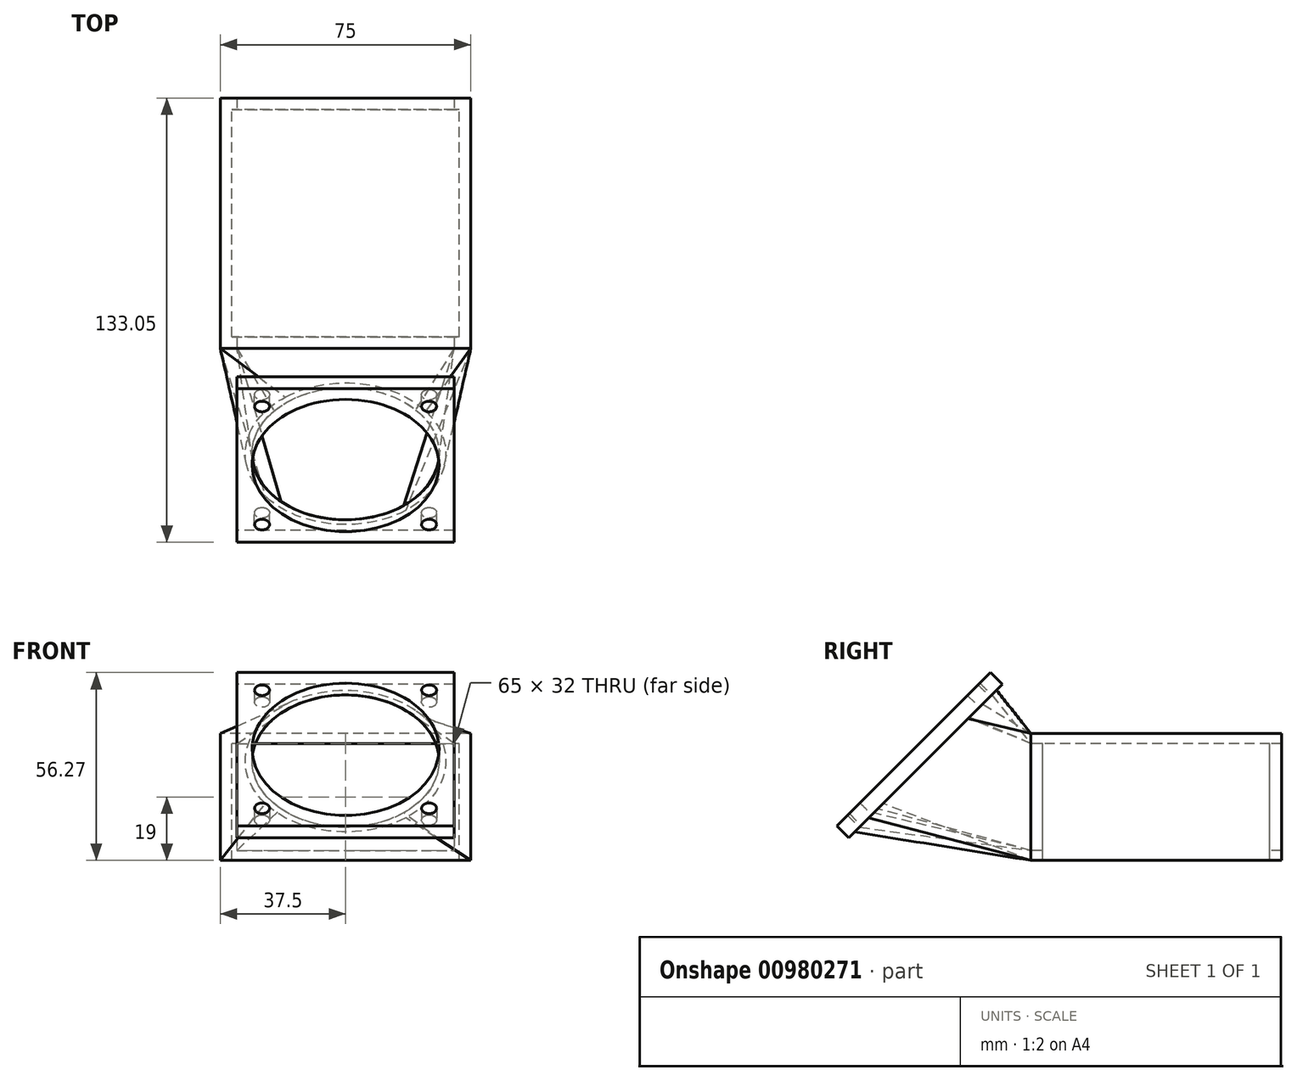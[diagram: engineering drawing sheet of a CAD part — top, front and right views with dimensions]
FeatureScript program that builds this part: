
annotation { "Feature Type Name" : "Feature", "Feature Type Description" : "" }
export const myFeature = defineFeature(function(context is Context, id is Id, definition is map)
    precondition{}
    {
        {
            var Q0;
            Q0=qCreatedBy(makeId("Top.planeOp"),FACE);
            cPlane(context, id + "F0", {"entities" : qUnion([Q0]), "cplaneType" : CPlaneType.OFFSET, "offset" : 3 * mm, "width" : 152.4 * mm, "height" : 152.4 * mm});
        }
        {
            var Q0;
            Q0=qCreatedBy(id+"F0.planeOp",FACE);
            var sketch = newSketch(context, id + "F1", { "sketchPlane" : qUnion([Q0])});
            skLineSegment(sketch, "E0.bottom", {"start": v(37.5, -37.5) * mm, "end": v(-37.5, -37.5) * mm});
            skLineSegment(sketch, "E0.top", {"start": v(37.5, 37.5) * mm, "end": v(-37.5, 37.5) * mm});
            skLineSegment(sketch, "E0.left", {"start": v(37.5, -37.5) * mm, "end": v(37.5, 37.5) * mm});
            skLineSegment(sketch, "E0.right", {"start": v(-37.5, -37.5) * mm, "end": v(-37.5, 37.5) * mm});
            skPoint(sketch, "E0.middle", {"position": v(0, 0) * mm});
            skSolve(sketch);
        }
        {
            var Q0;
            Q0=makeQuery(id+"F1.imprint","IMPRINT",FACE,{"disambiguationData":[TD([[makeQuery(id+"F1.imprint","IMPRINT",EDGE,{"derivedFrom":sQuery(id+"F1.wireOp",EDGE,"E0.bottom")}),-1.0]])]});
            extrude(context, id + "F2", {"entities" : qUnion([Q0]), "oppositeDirection" : true, "depth" : 38 * mm, "offsetDistance" : 25 * mm});
        }
        {
            var Q0;
            Q0=qCreatedBy(makeId("Top.planeOp"),FACE);
            var sketch = newSketch(context, id + "F3", { "sketchPlane" : qUnion([Q0])});
            skPoint(sketch, "E1.middle", {"position": v(0, 0) * mm});
            skLineSegment(sketch, "E2.bottom", {"start": v(34, 34) * mm, "end": v(-34, 34) * mm});
            skLineSegment(sketch, "E2.top", {"start": v(34, -34) * mm, "end": v(-34, -34) * mm});
            skLineSegment(sketch, "E2.left", {"start": v(34, 34) * mm, "end": v(34, -34) * mm});
            skLineSegment(sketch, "E2.right", {"start": v(-34, 34) * mm, "end": v(-34, -34) * mm});
            skSolve(sketch);
        }
        {
            var Q0;
            Q0 = qSketchRegion(id + "F3", true);
            var Q1;
            Q1=makeQuery(id+"F2.opExtrude","CAP_FACE",FACE,{"disambiguationData":[OSD([sQuery(id+"F1.wireOp",EDGE,"E0.bottom"),sQuery(id+"F1.wireOp",EDGE,"E0.top"),sQuery(id+"F1.wireOp",EDGE,"E0.left"),sQuery(id+"F1.wireOp",EDGE,"E0.right")])],"isStart":false});
            extrude(context, id + "F4", {"entities" : qUnion([Q0]), "endBound" : BoundingType.UP_TO_SURFACE, "oppositeDirection" : true, "depth" : 70 * mm, "endBoundEntityFace" : qUnion([Q1]), "offsetDistance" : 25 * mm});
        }
        {
            var Q0;
            Q0=makeQuery(id+"F4.opExtrude","SWEPT_BODY",BODY,{"disambiguationData":[OSD([sQuery(id+"F3.wireOp",EDGE,"E2.bottom"),sQuery(id+"F3.wireOp",EDGE,"E2.top"),sQuery(id+"F3.wireOp",EDGE,"E2.left"),sQuery(id+"F3.wireOp",EDGE,"E2.right")])]});
            var Q1;
            Q1=makeQuery(id+"F2.opExtrude","SWEPT_BODY",BODY,{"disambiguationData":[OSD([sQuery(id+"F1.wireOp",EDGE,"E0.bottom"),sQuery(id+"F1.wireOp",EDGE,"E0.top"),sQuery(id+"F1.wireOp",EDGE,"E0.left"),sQuery(id+"F1.wireOp",EDGE,"E0.right")])]});
            booleanBodies(context, id + "F5", {"operationType" : BooleanOperationType.SUBTRACTION, "tools" : qUnion([Q0]), "targets" : qUnion([Q1])});
        }
        {
            var Q0;
            Q0=makeQuery(id+"F2.opExtrude","SWEPT_FACE",FACE,{"disambiguationData":[OSD([sQuery(id+"F1.wireOp",EDGE,"E0.bottom")])]});
            var sketch = newSketch(context, id + "F6", { "sketchPlane" : qUnion([Q0])});
            skLineSegment(sketch, "E3.bottom", {"start": v(-32.5, 0) * mm, "end": v(32.5, 0) * mm});
            skLineSegment(sketch, "E3.top", {"start": v(-32.5, -32) * mm, "end": v(32.5, -32) * mm});
            skLineSegment(sketch, "E3.left", {"start": v(-32.5, 0) * mm, "end": v(-32.5, -32) * mm});
            skLineSegment(sketch, "E3.right", {"start": v(32.5, 0) * mm, "end": v(32.5, -32) * mm});
            skPoint(sketch, "E3.middle", {"position": v(0, -16) * mm});
            skPoint(sketch, "E3.centerSnap0", {"position": v(36.5, -16) * mm});
            skPoint(sketch, "E3.centerSnap1", {"position": v(0, 32.87) * mm});
            skSolve(sketch);
        }
        {
            var Q0;
            Q0=makeQuery(id+"F6.imprint","IMPRINT",FACE,{"disambiguationData":[TD([[makeQuery(id+"F6.imprint","IMPRINT",EDGE,{"derivedFrom":sQuery(id+"F6.wireOp",EDGE,"E3.bottom")}),-1.0]])]});
            var Q1;
            Q1=makeQuery(id+"F2.opExtrude","SWEPT_FACE",FACE,{"disambiguationData":[OSD([sQuery(id+"F1.wireOp",EDGE,"E0.top")])]});
            extrude(context, id + "F7", {"entities" : qUnion([Q0]), "endBound" : BoundingType.UP_TO_SURFACE, "oppositeDirection" : true, "depth" : 25 * mm, "endBoundEntityFace" : qUnion([Q1]), "offsetDistance" : 25 * mm});
        }
        {
            var Q0;
            Q0=makeQuery(id+"F7.opExtrude","SWEPT_BODY",BODY,{"disambiguationData":[OSD([sQuery(id+"F6.wireOp",EDGE,"E3.bottom"),sQuery(id+"F6.wireOp",EDGE,"E3.top"),sQuery(id+"F6.wireOp",EDGE,"E3.left"),sQuery(id+"F6.wireOp",EDGE,"E3.right")])]});
            var Q1;
            Q1=makeQuery(id+"F2.opExtrude","SWEPT_BODY",BODY,{"disambiguationData":[OSD([sQuery(id+"F1.wireOp",EDGE,"E0.bottom"),sQuery(id+"F1.wireOp",EDGE,"E0.top"),sQuery(id+"F1.wireOp",EDGE,"E0.left"),sQuery(id+"F1.wireOp",EDGE,"E0.right")])]});
            booleanBodies(context, id + "F8", {"operationType" : BooleanOperationType.SUBTRACTION, "tools" : qUnion([Q0]), "targets" : qUnion([Q1])});
        }
        {
            var Q0;
            Q0=makeQuery(id+"F2.opExtrude","SWEPT_FACE",FACE,{"disambiguationData":[OSD([sQuery(id+"F1.wireOp",EDGE,"E0.bottom")])]});
            var sketch = newSketch(context, id + "F9", { "sketchPlane" : qUnion([Q0])});
            skLineSegment(sketch, "E4.bottom", {"start": v(-32.5, -32) * mm, "end": v(32.5, -32) * mm});
            skLineSegment(sketch, "E4.top", {"start": v(-32.5, 0) * mm, "end": v(32.5, 0) * mm});
            skLineSegment(sketch, "E4.left", {"start": v(-32.5, -32) * mm, "end": v(-32.5, 0) * mm});
            skLineSegment(sketch, "E4.right", {"start": v(32.5, -32) * mm, "end": v(32.5, 0) * mm});
            skSolve(sketch);
        }
        {
            var Q0;
            Q0=makeQuery(id+"F2.opExtrude","SWEPT_FACE",FACE,{"disambiguationData":[OSD([sQuery(id+"F1.wireOp",EDGE,"E0.bottom")])]});
            var sketch = newSketch(context, id + "F10", { "sketchPlane" : qUnion([Q0])});
            skLineSegment(sketch, "E5.bottom", {"start": v(-37.5, 3) * mm, "end": v(37.5, 3) * mm});
            skLineSegment(sketch, "E5.top", {"start": v(-37.5, -35) * mm, "end": v(37.5, -35) * mm});
            skLineSegment(sketch, "E5.left", {"start": v(-37.5, 3) * mm, "end": v(-37.5, -35) * mm});
            skLineSegment(sketch, "E5.right", {"start": v(37.5, 3) * mm, "end": v(37.5, -35) * mm});
            skSolve(sketch);
        }
        {
            var Q0;
            Q0=makeQuery(id+"F10.imprint","IMPRINT",FACE,{"disambiguationData":[TD([[makeQuery(id+"F10.imprint","IMPRINT",EDGE,{"derivedFrom":sQuery(id+"F10.wireOp",EDGE,"E5.bottom")}),1.0]])]});
            var sketch = newSketch(context, id + "F11", { "sketchPlane" : qUnion([Q0])});
            skLineSegment(sketch, "E6", {"start": v(-64.88, -2) * mm, "end": v(64.63, -2) * mm, "construction": true});
            skSolve(sketch);
        }
        {
            var Q0;
            Q0=sQuery(id+"F11.wireOp",EDGE,"E6");
            cPlane(context, id + "F12", {"entities" : qUnion([Q0]), "cplaneType" : CPlaneType.LINE_ANGLE, "offset" : 80 * mm, "angle" : 45 * degree, "oppositeDirection" : true, "width" : 150 * mm, "height" : 150 * mm});
        }
        {
            var Q0;
            Q0=qCreatedBy(id+"F12.planeOp",FACE);
            cPlane(context, id + "F13", {"entities" : qUnion([Q0]), "cplaneType" : CPlaneType.OFFSET, "offset" : 20 * mm, "oppositeDirection" : true, "width" : 150 * mm, "height" : 150 * mm});
        }
        {
            var Q0;
            Q0=qCreatedBy(id+"F13.planeOp",FACE);
            var sketch = newSketch(context, id + "F14", { "sketchPlane" : qUnion([Q0])});
            skArc(sketch, "E7", {"start": v(21.34, -34.4) * mm, "mid": v(0.3, -24.52) * mm, "end": v(-20.95, -33.94) * mm});
            skArc(sketch, "E8", {"start": v(-20.95, -33.94) * mm, "mid": v(-27.9, -55) * mm, "end": v(-17.35, -74.5) * mm});
            skArc(sketch, "E9", {"start": v(-17.35, -74.5) * mm, "mid": v(1.34, -80.49) * mm, "end": v(19.38, -72.73) * mm});
            skArc(sketch, "E10", {"start": v(19.38, -72.73) * mm, "mid": v(27.96, -53.95) * mm, "end": v(21.34, -34.4) * mm});
            skSolve(sketch);
        }
        {
            var Q0;
            Q0=makeQuery(id+"F9.imprint","IMPRINT",FACE,{"disambiguationData":[TD([[makeQuery(id+"F9.imprint","IMPRINT",EDGE,{"derivedFrom":sQuery(id+"F9.wireOp",EDGE,"E4.bottom")}),1.0]])]});
            var Q1;
            Q1 = qSketchRegion(id + "F14", true);
            loft(context, id + "F15", {"sheetProfilesArray" : [{ "sheetProfileEntities" : qUnion([Q0]) }, { "sheetProfileEntities" : qUnion([Q1]) }]});
        }
        {
            var Q0;
            Q0=qCreatedBy(id+"F13.planeOp",FACE);
            var sketch = newSketch(context, id + "F16", { "sketchPlane" : qUnion([Q0])});
            skCircle(sketch, "E11", {"center": v(0, -52.52) * mm, "radius": 30 * mm});
            skSolve(sketch);
        }
        {
            var Q0;
            Q0 = qSketchRegion(id + "F10", true);
            var Q1;
            Q1 = qSketchRegion(id + "F16", true);
            loft(context, id + "F17", {"sheetProfilesArray" : [{ "sheetProfileEntities" : qUnion([Q0]) }, { "sheetProfileEntities" : qUnion([Q1]) }]});
        }
        {
            var Q0;
            Q0 = qSketchRegion(id + "F14", true);
            extrude(context, id + "F18", {"entities" : qUnion([Q0]), "oppositeDirection" : true, "depth" : 5 * mm, "offsetDistance" : 25 * mm});
        }
        {
            var Q0;
            Q0=qCreatedBy(id+"F13.planeOp",FACE);
            var sketch = newSketch(context, id + "F19", { "sketchPlane" : qUnion([Q0])});
            skLineSegment(sketch, "E12.bottom", {"start": v(-32.5, -85.02) * mm, "end": v(32.5, -85.02) * mm});
            skLineSegment(sketch, "E12.top", {"start": v(-32.5, -20.02) * mm, "end": v(32.5, -20.02) * mm});
            skLineSegment(sketch, "E12.left", {"start": v(-32.5, -85.02) * mm, "end": v(-32.5, -20.02) * mm});
            skLineSegment(sketch, "E12.right", {"start": v(32.5, -85.02) * mm, "end": v(32.5, -20.02) * mm});
            skPoint(sketch, "E12.middle", {"position": v(0, -52.52) * mm});
            skSolve(sketch);
        }
        {
            var Q0;
            Q0=makeQuery(id+"F19.imprint","IMPRINT",FACE,{"disambiguationData":[TD([[makeQuery(id+"F19.imprint","IMPRINT",EDGE,{"derivedFrom":sQuery(id+"F19.wireOp",EDGE,"E12.bottom")}),1.0]])]});
            var sketch = newSketch(context, id + "F20", { "sketchPlane" : qUnion([Q0])});
            skLineSegment(sketch, "E13", {"start": v(32.5, -20.02) * mm, "end": v(-32.5, -85.02) * mm, "construction": true});
            skLineSegment(sketch, "E14", {"start": v(-32.5, -20.02) * mm, "end": v(37.47, -90) * mm, "construction": true});
            skLineSegment(sketch, "E15.bottom", {"start": v(25, -27.52) * mm, "end": v(-25, -27.52) * mm, "construction": true});
            skLineSegment(sketch, "E15.top", {"start": v(25, -77.52) * mm, "end": v(-25, -77.52) * mm, "construction": true});
            skLineSegment(sketch, "E15.left", {"start": v(25, -27.52) * mm, "end": v(25, -77.52) * mm, "construction": true});
            skLineSegment(sketch, "E15.right", {"start": v(-25, -27.52) * mm, "end": v(-25, -77.52) * mm, "construction": true});
            skPoint(sketch, "E15.middle", {"position": v(0, -52.52) * mm});
            skSolve(sketch);
        }
        {
            var Q0;
            Q0=makeQuery(id+"F19.imprint","IMPRINT",FACE,{"disambiguationData":[TD([[makeQuery(id+"F19.imprint","IMPRINT",EDGE,{"derivedFrom":sQuery(id+"F19.wireOp",EDGE,"E12.bottom")}),1.0]])]});
            var sketch = newSketch(context, id + "F21", { "sketchPlane" : qUnion([Q0])});
            skCircle(sketch, "E16", {"center": v(-25, -27.52) * mm, "radius": 2.25 * mm});
            skCircle(sketch, "E17", {"center": v(25, -27.52) * mm, "radius": 2.25 * mm});
            skCircle(sketch, "E18", {"center": v(25, -77.52) * mm, "radius": 2.25 * mm});
            skCircle(sketch, "E19", {"center": v(-25, -77.52) * mm, "radius": 2.25 * mm});
            skSolve(sketch);
        }
        {
            var Q0;
            Q0 = qSketchRegion(id + "F21", true);
            extrude(context, id + "F22", {"entities" : qUnion([Q0]), "oppositeDirection" : true, "depth" : 5 * mm, "offsetDistance" : 25 * mm});
        }
        {
            var Q0;
            Q0=makeQuery(id+"F19.imprint","IMPRINT",FACE,{"disambiguationData":[TD([[makeQuery(id+"F19.imprint","IMPRINT",EDGE,{"derivedFrom":sQuery(id+"F19.wireOp",EDGE,"E12.bottom")}),1.0]])]});
            var Q1;
            Q1 = qSketchRegion(id + "F3", true);
            extrude(context, id + "F23", {"entities" : qUnion([Q0, Q1]), "oppositeDirection" : true, "depth" : 5 * mm, "offsetDistance" : 25 * mm});
        }
        {
            var Q0;
            Q0=makeQuery(id+"F22.opExtrude","SWEPT_BODY",BODY,{"disambiguationData":[OSD([sQuery(id+"F21.wireOp",EDGE,"E16")])]});
            var Q1;
            Q1=makeQuery(id+"F22.opExtrude","SWEPT_BODY",BODY,{"disambiguationData":[OSD([sQuery(id+"F21.wireOp",EDGE,"E17")])]});
            var Q2;
            Q2=makeQuery(id+"F22.opExtrude","SWEPT_BODY",BODY,{"disambiguationData":[OSD([sQuery(id+"F21.wireOp",EDGE,"E18")])]});
            var Q3;
            Q3=makeQuery(id+"F22.opExtrude","SWEPT_BODY",BODY,{"disambiguationData":[OSD([sQuery(id+"F21.wireOp",EDGE,"E19")])]});
            var Q4;
            Q4=makeQuery(id+"F18.opExtrude","SWEPT_BODY",BODY,{"disambiguationData":[OSD([sQuery(id+"F14.wireOp",EDGE,"E7"),sQuery(id+"F14.wireOp",EDGE,"E8"),sQuery(id+"F14.wireOp",EDGE,"E9"),sQuery(id+"F14.wireOp",EDGE,"E10")])]});
            var Q5;
            Q5=makeQuery(id+"F23.opExtrude","SWEPT_BODY",BODY,{"disambiguationData":[OSD([sQuery(id+"F19.wireOp",EDGE,"E12.bottom"),sQuery(id+"F19.wireOp",EDGE,"E12.top"),sQuery(id+"F19.wireOp",EDGE,"E12.left"),sQuery(id+"F19.wireOp",EDGE,"E12.right")])]});
            booleanBodies(context, id + "F24", {"operationType" : BooleanOperationType.SUBTRACTION, "tools" : qUnion([Q0, Q1, Q2, Q3, Q4]), "targets" : qUnion([Q5])});
        }
        {
            var Q0;
            Q0=makeQuery(id+"F15.opLoft","SWEPT_BODY",BODY,{"disambiguationData":[OSD([makeQuery(id+"F9.imprint","IMPRINT",FACE,{"disambiguationData":[TD([[makeQuery(id+"F9.imprint","IMPRINT",EDGE,{"derivedFrom":sQuery(id+"F9.wireOp",EDGE,"E4.bottom")}),1.0]])]}),makeQuery(id+"F14.imprint","IMPRINT",FACE,{"disambiguationData":[TD([[makeQuery(id+"F14.imprint","IMPRINT",EDGE,{"derivedFrom":sQuery(id+"F14.wireOp",EDGE,"E7")}),1.0]])]})])]});
            var Q1;
            Q1=makeQuery(id+"F17.opLoft","SWEPT_BODY",BODY,{"disambiguationData":[OSD([makeQuery(id+"F10.imprint","IMPRINT",FACE,{"disambiguationData":[TD([[makeQuery(id+"F10.imprint","IMPRINT",EDGE,{"derivedFrom":sQuery(id+"F10.wireOp",EDGE,"E5.bottom")}),1.0]])]}),makeQuery(id+"F19.imprint","IMPRINT",FACE,{"disambiguationData":[TD([[makeQuery(id+"F19.imprint","IMPRINT",EDGE,{"derivedFrom":sQuery(id+"F19.wireOp",EDGE,"E12.bottom")}),1.0]])]})])]});
            booleanBodies(context, id + "F25", {"operationType" : BooleanOperationType.SUBTRACTION, "tools" : qUnion([Q0]), "targets" : qUnion([Q1])});
        }
        {
            var Q0;
            Q0=makeQuery(id+"F23.opExtrude","SWEPT_BODY",BODY,{"disambiguationData":[OSD([sQuery(id+"F3.wireOp",EDGE,"E2.bottom"),sQuery(id+"F3.wireOp",EDGE,"E2.top"),sQuery(id+"F3.wireOp",EDGE,"E2.left"),sQuery(id+"F3.wireOp",EDGE,"E2.right")])]});
            deleteBodies(context, id + "F26", {"entities" : qUnion([Q0])});
        }
    });
